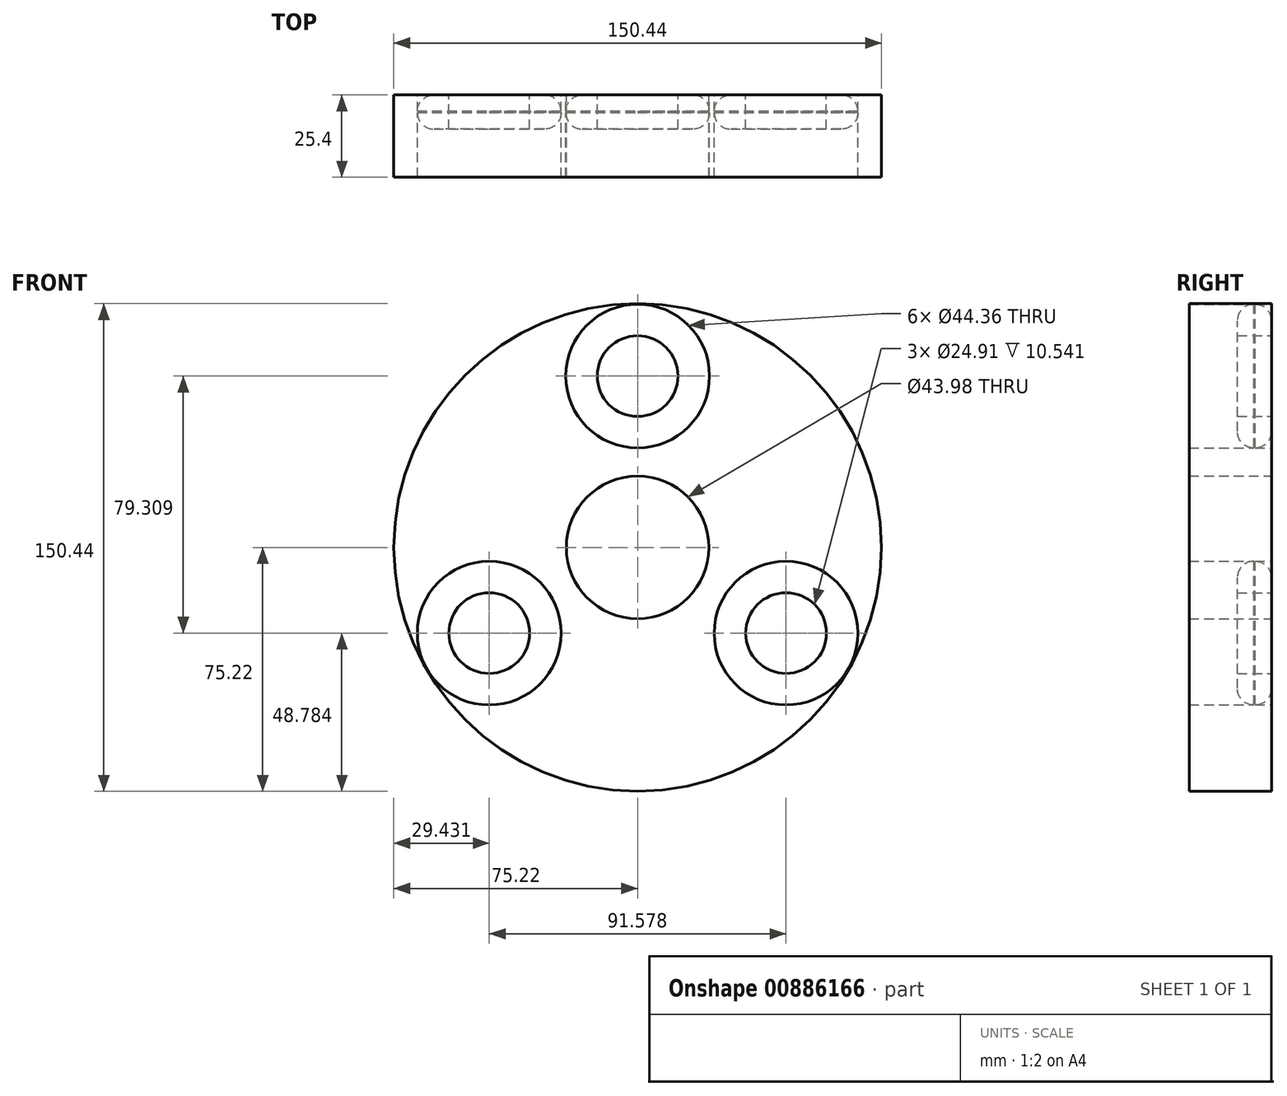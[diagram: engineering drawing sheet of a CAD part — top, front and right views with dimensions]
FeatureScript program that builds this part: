
annotation { "Feature Type Name" : "Feature", "Feature Type Description" : "" }
export const myFeature = defineFeature(function(context is Context, id is Id, definition is map)
    precondition{}
    {
        {
            var Q0;
            Q0=qCreatedBy(makeId("Front.planeOp"),FACE);
            var sketch = newSketch(context, id + "F0", { "sketchPlane" : qUnion([Q0])});
            skCircle(sketch, "E0", {"center": v(0, 0) * mm, "radius": 75.22 * mm});
            skCircle(sketch, "E1", {"center": v(0, 0) * mm, "radius": 22 * mm});
            skCircle(sketch, "E2", {"center": v(0, 52.87) * mm, "radius": 12.46 * mm});
            skCircle(sketch, "E3", {"center": v(0, 52.87) * mm, "radius": 22.18 * mm});
            skCircle(sketch, "E4.1.0", {"center": v(-45.79, -26.44) * mm, "radius": 22.18 * mm});
            skCircle(sketch, "E4.2.0", {"center": v(45.79, -26.44) * mm, "radius": 22.18 * mm});
            skCircle(sketch, "E5.1.0", {"center": v(-45.79, -26.44) * mm, "radius": 12.46 * mm});
            skCircle(sketch, "E5.2.0", {"center": v(45.79, -26.44) * mm, "radius": 12.46 * mm});
            skCircle(sketch, "E6", {"center": v(0, 0) * mm, "radius": 13.46 * mm});
            skSolve(sketch);
        }
        {
            var Q0;
            Q0=makeQuery(id+"F0.imprint","IMPRINT",FACE,{"disambiguationData":[TD([[makeQuery(id+"F0.imprint","IMPRINT",EDGE,{"derivedFrom":sQuery(id+"F0.wireOp",EDGE,"E0")}),1.0]])]});
            var sketch = newSketch(context, id + "F1", { "sketchPlane" : qUnion([Q0])});
            skLineSegment(sketch, "E7", {"start": v(-16.72, 38.32) * mm, "end": v(-40.98, -4.8) * mm});
            skLineSegment(sketch, "E8.1.0", {"start": v(-24.83, -33.64) * mm, "end": v(24.64, -33.09) * mm});
            skLineSegment(sketch, "E8.2.0", {"start": v(41.55, -4.68) * mm, "end": v(16.33, 37.88) * mm});
            skPoint(sketch, "E8.center", {"position": v(0, 0) * mm});
            skSolve(sketch);
        }
        {
            var Q0;
            Q0=makeQuery(id+"F1.imprint","IMPRINT",FACE,{"disambiguationData":[TD([[makeQuery(id+"F1.imprint","IMPRINT",EDGE,{"derivedFrom":makeQuery(id+"F0.imprint","IMPRINT",EDGE,{"derivedFrom":sQuery(id+"F0.wireOp",EDGE,"E1")})}),-1.0]])]});
            var Q1;
            Q1=makeQuery(id+"F0.imprint","IMPRINT",FACE,{"disambiguationData":[TD([[makeQuery(id+"F0.imprint","IMPRINT",EDGE,{"derivedFrom":sQuery(id+"F0.wireOp",EDGE,"E2")}),-1.0]])]});
            var Q2;
            Q2=makeQuery(id+"F0.imprint","IMPRINT",FACE,{"disambiguationData":[TD([[makeQuery(id+"F0.imprint","IMPRINT",EDGE,{"derivedFrom":sQuery(id+"F0.wireOp",EDGE,"E4.1.0")}),1.0]])]});
            var Q3;
            Q3=makeQuery(id+"F0.imprint","IMPRINT",FACE,{"disambiguationData":[TD([[makeQuery(id+"F0.imprint","IMPRINT",EDGE,{"derivedFrom":sQuery(id+"F0.wireOp",EDGE,"E4.2.0")}),1.0]])]});
            extrude(context, id + "F2", {"entities" : qUnion([Q0, Q1, Q2, Q3]), "depth" : 10.54 * mm, "offsetDistance" : 25.4 * mm});
        }
        {
            var Q0;
            {var subQ0=sQuery(id+"F0.wireOp",EDGE,"E3");Q0=makeQuery(id+"F2.opExtrude","CAP_EDGE",EDGE,{"disambiguationData":[OSD([subQ0]),TDD([makeQuery(id+"F0.imprint","IMPRINT",EDGE,{"derivedFrom":subQ0})])],"isStart":false});}
            fillet(context, id + "F3", {"entities" : qUnion([Q0]), "radius" : 5.08 * mm, "tangentPropagation" : true, "allowEdgeOverflow" : false});
        }
        {
            var Q0;
            {var subQ0=sQuery(id+"F0.wireOp",EDGE,"E4.1.0");Q0=makeQuery(id+"F2.opExtrude","CAP_EDGE",EDGE,{"disambiguationData":[OSD([subQ0]),TDD([makeQuery(id+"F0.imprint","IMPRINT",EDGE,{"derivedFrom":subQ0})])],"isStart":false});}
            var Q1;
            {var subQ0=sQuery(id+"F0.wireOp",EDGE,"E4.2.0");Q1=makeQuery(id+"F2.opExtrude","CAP_EDGE",EDGE,{"disambiguationData":[OSD([subQ0]),TDD([makeQuery(id+"F0.imprint","IMPRINT",EDGE,{"derivedFrom":subQ0})])],"isStart":false});}
            var Q2;
            Q2=makeQuery(id+"F2.opExtrude","CAP_EDGE",EDGE,{"disambiguationData":[OSD([sQuery(id+"F1.wireOp",EDGE,"E8.2.0")])],"isStart":false});
            var Q3;
            Q3=makeQuery(id+"F2.opExtrude","CAP_EDGE",EDGE,{"disambiguationData":[OSD([sQuery(id+"F1.wireOp",EDGE,"E8.1.0")])],"isStart":false});
            var Q4;
            Q4=makeQuery(id+"F2.opExtrude","CAP_EDGE",EDGE,{"disambiguationData":[OSD([sQuery(id+"F1.wireOp",EDGE,"E7")])],"isStart":false});
            fillet(context, id + "F4", {"entities" : qUnion([Q0, Q1, Q2, Q3, Q4]), "radius" : 5.08 * mm, "tangentPropagation" : true, "allowEdgeOverflow" : false});
        }
        {
            var Q0;
            {var subQ0=sQuery(id+"F0.wireOp",EDGE,"E4.1.0");Q0=makeQuery(id+"F2.opExtrude","CAP_EDGE",EDGE,{"disambiguationData":[OSD([subQ0]),TDD([makeQuery(id+"F0.imprint","IMPRINT",EDGE,{"derivedFrom":subQ0})])],"isStart":true});}
            var Q1;
            {var subQ0=sQuery(id+"F0.wireOp",EDGE,"E3");Q1=makeQuery(id+"F2.opExtrude","CAP_EDGE",EDGE,{"disambiguationData":[OSD([subQ0]),TDD([makeQuery(id+"F0.imprint","IMPRINT",EDGE,{"derivedFrom":subQ0})])],"isStart":true});}
            var Q2;
            {var subQ0=sQuery(id+"F0.wireOp",EDGE,"E4.2.0");Q2=makeQuery(id+"F2.opExtrude","CAP_EDGE",EDGE,{"disambiguationData":[OSD([subQ0]),TDD([makeQuery(id+"F0.imprint","IMPRINT",EDGE,{"derivedFrom":subQ0})])],"isStart":true});}
            var Q3;
            Q3=makeQuery(id+"F2.opExtrude","CAP_EDGE",EDGE,{"disambiguationData":[OSD([sQuery(id+"F1.wireOp",EDGE,"E8.2.0")])],"isStart":true});
            var Q4;
            Q4=makeQuery(id+"F2.opExtrude","CAP_EDGE",EDGE,{"disambiguationData":[OSD([sQuery(id+"F1.wireOp",EDGE,"E8.1.0")])],"isStart":true});
            var Q5;
            Q5=makeQuery(id+"F2.opExtrude","CAP_EDGE",EDGE,{"disambiguationData":[OSD([sQuery(id+"F1.wireOp",EDGE,"E7")])],"isStart":true});
            fillet(context, id + "F5", {"entities" : qUnion([Q0, Q1, Q2, Q3, Q4, Q5]), "radius" : 5.08 * mm, "tangentPropagation" : true, "allowEdgeOverflow" : false});
        }
        {
            var Q0;
            Q0 = qSketchRegion(id + "F0", true);
            extrude(context, id + "F6", {"entities" : qUnion([Q0]), "operationType" : NewBodyOperationType.ADD, "depth" : 25.4 * mm, "offsetDistance" : 25.4 * mm});
        }
    });
